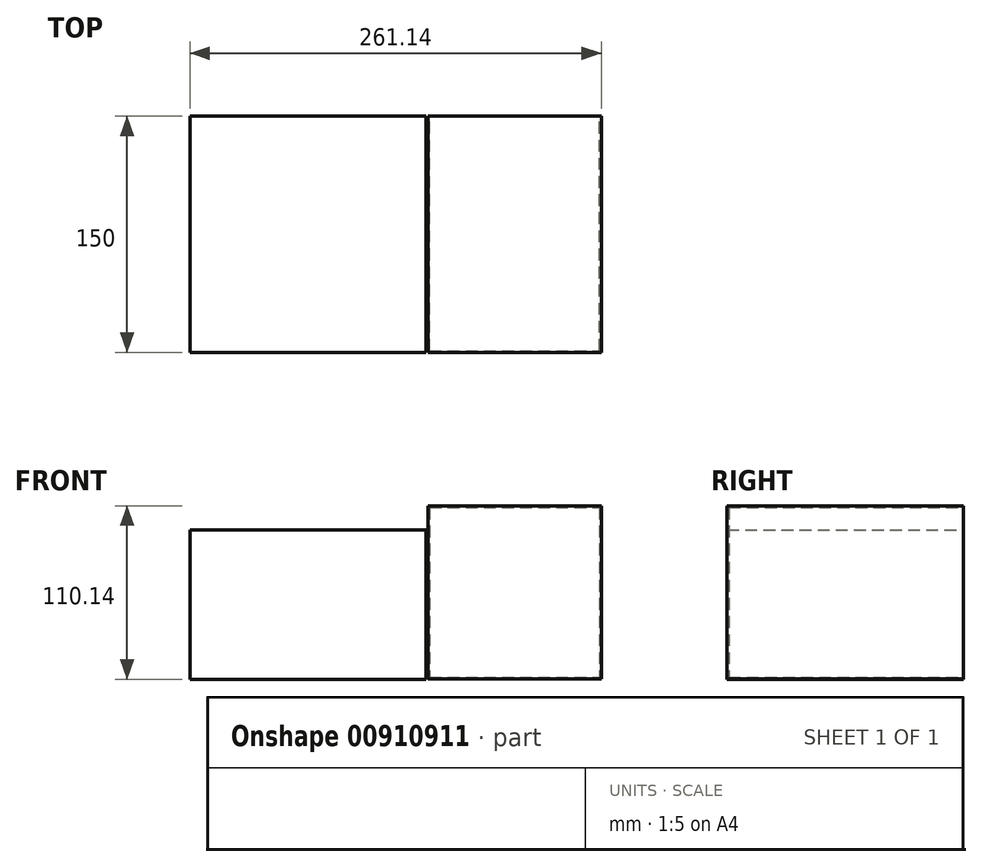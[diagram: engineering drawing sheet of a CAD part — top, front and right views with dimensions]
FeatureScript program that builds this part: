
annotation { "Feature Type Name" : "Feature", "Feature Type Description" : "" }
export const myFeature = defineFeature(function(context is Context, id is Id, definition is map)
    precondition{}
    {
        {
            var Q0;
            Q0=qCreatedBy(makeId("Front.planeOp"),FACE);
            var sketch = newSketch(context, id + "F0", { "sketchPlane" : qUnion([Q0])});
            skLineSegment(sketch, "E0.bottom", {"start": v(27.5, -15.8) * mm, "end": v(-122.5, -15.8) * mm});
            skLineSegment(sketch, "E0.top", {"start": v(27.5, -110.8) * mm, "end": v(-122.5, -110.8) * mm});
            skLineSegment(sketch, "E0.left", {"start": v(27.5, -15.8) * mm, "end": v(27.5, -110.8) * mm});
            skLineSegment(sketch, "E0.right", {"start": v(-122.5, -15.8) * mm, "end": v(-122.5, -110.8) * mm});
            skSolve(sketch);
        }
        {
            var Q0;
            Q0 = qSketchRegion(id + "F0", true);
            extrude(context, id + "F1", {"entities" : qUnion([Q0]), "endBound" : BoundingType.SYMMETRIC, "depth" : 150 * mm, "offsetDistance" : 25 * mm});
        }
        {
            var Q0;
            Q0=qCreatedBy(makeId("Front.planeOp"),FACE);
            var sketch = newSketch(context, id + "F2", { "sketchPlane" : qUnion([Q0])});
            skLineSegment(sketch, "E1.bottom", {"start": v(28.64, -0.66) * mm, "end": v(138.64, -0.66) * mm});
            skLineSegment(sketch, "E1.top", {"start": v(28.64, -110.66) * mm, "end": v(138.64, -110.66) * mm});
            skLineSegment(sketch, "E1.left", {"start": v(28.64, -0.66) * mm, "end": v(28.64, -110.66) * mm});
            skLineSegment(sketch, "E1.right", {"start": v(138.64, -0.66) * mm, "end": v(138.64, -110.66) * mm});
            skSolve(sketch);
        }
        {
            var Q0;
            Q0 = qSketchRegion(id + "F2", true);
            extrude(context, id + "F3", {"entities" : qUnion([Q0]), "endBound" : BoundingType.SYMMETRIC, "depth" : 150 * mm, "offsetDistance" : 25 * mm});
        }
        {
            var Q0;
            Q0=makeQuery(id+"F3.opExtrude","CAP_FACE",FACE,{"disambiguationData":[OSD([sQuery(id+"F2.wireOp",EDGE,"E1.bottom"),sQuery(id+"F2.wireOp",EDGE,"E1.top"),sQuery(id+"F2.wireOp",EDGE,"E1.left"),sQuery(id+"F2.wireOp",EDGE,"E1.right")])],"isStart":true});
            shell(context, id + "F4", {"entities" : qUnion([Q0]), "thickness" : 1 * mm});
        }
    });
